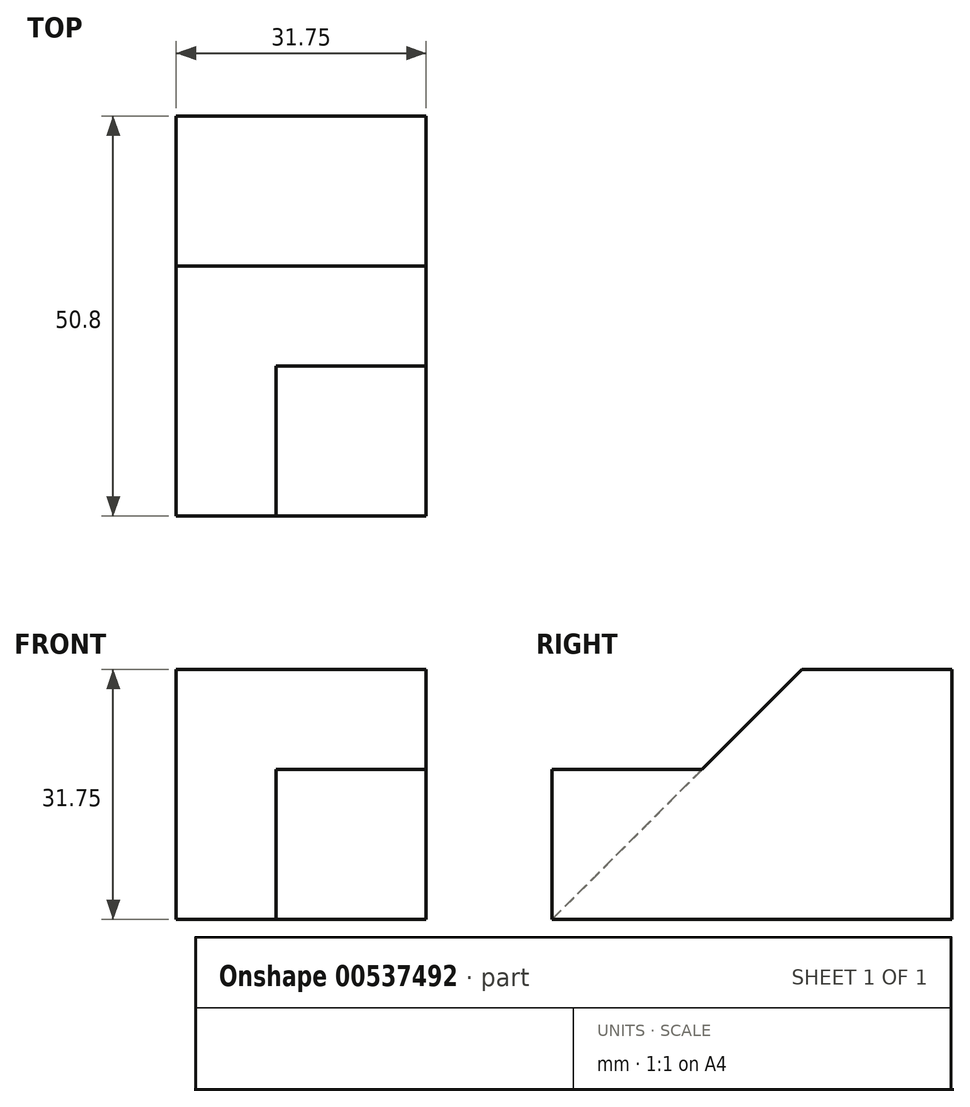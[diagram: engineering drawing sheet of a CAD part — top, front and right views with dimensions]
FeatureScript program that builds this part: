
annotation { "Feature Type Name" : "Feature", "Feature Type Description" : "" }
export const myFeature = defineFeature(function(context is Context, id is Id, definition is map)
    precondition{}
    {
        {
            var Q0;
            Q0=qCreatedBy(makeId("Right.planeOp"),FACE);
            var sketch = newSketch(context, id + "F0", { "sketchPlane" : qUnion([Q0])});
            skLineSegment(sketch, "E0", {"start": v(0, 0) * mm, "end": v(0, 31.75) * mm});
            skLineSegment(sketch, "E1", {"start": v(0, 31.75) * mm, "end": v(-19.05, 31.75) * mm});
            skLineSegment(sketch, "E2", {"start": v(0, 0) * mm, "end": v(-50.8, 0) * mm});
            skLineSegment(sketch, "E3", {"start": v(-50.8, 0) * mm, "end": v(-50.8, 19.05) * mm});
            skLineSegment(sketch, "E4", {"start": v(-50.8, 19.05) * mm, "end": v(-31.75, 19.05) * mm});
            skLineSegment(sketch, "E5", {"start": v(-31.75, 19.05) * mm, "end": v(-19.05, 31.75) * mm});
            skSolve(sketch);
        }
        {
            var Q0;
            Q0 = qSketchRegion(id + "F0", true);
            extrude(context, id + "F1", {"entities" : qUnion([Q0]), "depth" : 31.75 * mm, "offsetDistance" : 25.4 * mm});
        }
        {
            var Q0;
            Q0=makeQuery(id+"F1.opExtrude","CAP_FACE",FACE,{"disambiguationData":[OSD([sQuery(id+"F0.wireOp",EDGE,"E0"),sQuery(id+"F0.wireOp",EDGE,"E1"),sQuery(id+"F0.wireOp",EDGE,"E2"),sQuery(id+"F0.wireOp",EDGE,"E3"),sQuery(id+"F0.wireOp",EDGE,"E4"),sQuery(id+"F0.wireOp",EDGE,"E5")])],"isStart":true});
            var sketch = newSketch(context, id + "F2", { "sketchPlane" : qUnion([Q0])});
            skLineSegment(sketch, "E6", {"start": v(31.75, 19.05) * mm, "end": v(50.8, 0) * mm});
            skSolve(sketch);
        }
        {
            var Q0;
            Q0 = qSketchRegion(id + "F2", true);
            var Q1;
            Q1=makeQuery(id+"F2.imprint","IMPRINT",FACE,{"disambiguationData":[TD([[makeQuery(id+"F2.imprint","IMPRINT",EDGE,{"derivedFrom":sQuery(id+"F2.wireOp",EDGE,"E6")}),1.0]])]});
            extrude(context, id + "F3", {"entities" : qUnion([Q0, Q1]), "operationType" : NewBodyOperationType.REMOVE, "oppositeDirection" : true, "depth" : 12.7 * mm, "offsetDistance" : 25.4 * mm});
        }
    });
